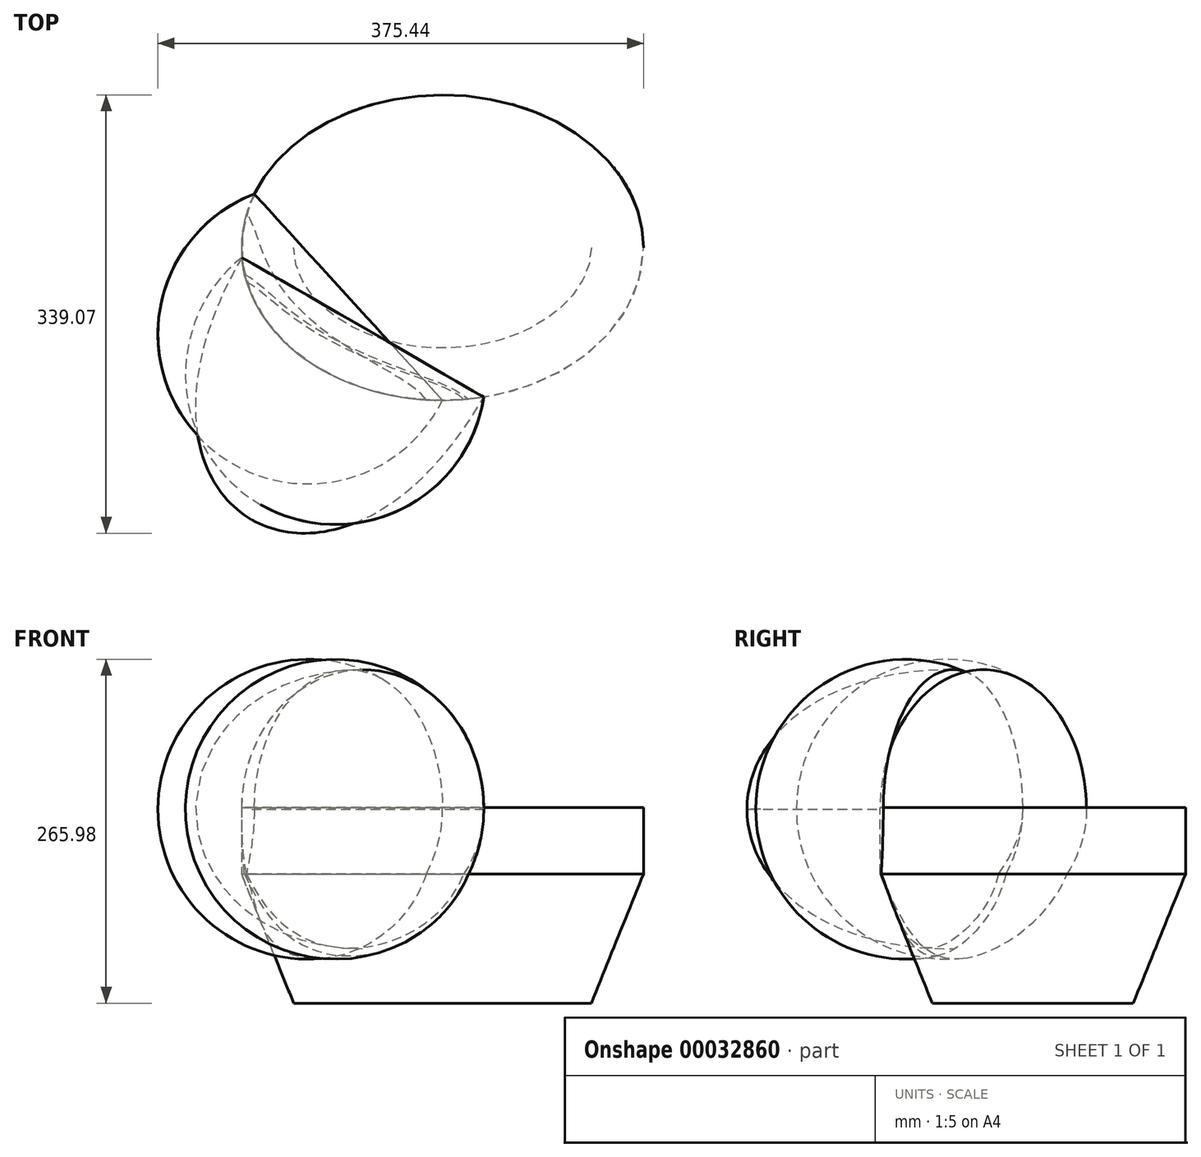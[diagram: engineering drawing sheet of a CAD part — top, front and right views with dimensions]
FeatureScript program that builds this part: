
annotation { "Feature Type Name" : "Feature", "Feature Type Description" : "" }
export const myFeature = defineFeature(function(context is Context, id is Id, definition is map)
    precondition{}
    {
        {
            assignVariable(context, id + "F0", {"name" : "DCM", "anyValue" : 21.6});
        }
        {
            var Q0;
            Q0=qCreatedBy(makeId("Top.planeOp"),FACE);
            var sketch = newSketch(context, id + "F1", { "sketchPlane" : qUnion([Q0])});
            skEllipse(sketch, "E0", {"center": v(0, 0) * mm, "majorRadius": 155.45 * mm, "minorRadius": 118.11 * mm, "majorAxis": v(1, 0)});
            skSolve(sketch);
        }
        {
            var Q0;
            Q0=qCreatedBy(makeId("Top.planeOp"),FACE);
            var sketch = newSketch(context, id + "F2", { "sketchPlane" : qUnion([Q0])});
            skEllipse(sketch, "E1", {"center": v(0, 0) * mm, "majorRadius": 155.45 * mm, "minorRadius": 118.11 * mm, "majorAxis": v(-1, 0)});
            skLineSegment(sketch, "E2", {"start": v(0, 0) * mm, "end": v(-177.32, -177.32) * mm, "construction": true});
            skLineSegment(sketch, "E3", {"start": v(-155.13, -7.6) * mm, "end": v(31.94, -115.6) * mm});
            skPoint(sketch, "E4", {"position": v(-61.6, -61.6) * mm});
            skEllipse(sketch, "E5", {"center": v(-61.6, -61.6) * mm, "majorRadius": 53 * mm, "minorRadius": 22.7 * mm, "majorAxis": v(-0.87, 0.5), "construction": true});
            skLineSegment(sketch, "E6", {"start": v(-61.6, -61.6) * mm, "end": v(-147.52, -210.43) * mm});
            skPoint(sketch, "E7", {"position": v(-94.04, -94.04) * mm});
            skFitSpline(sketch, "E8", {"points": [v(-155.13, -7.6) * mm, v(31.94, -115.6) * mm], "startDerivative": vector(-343.7, -595.35) * mm, "endDerivative": vector(343.7, 595.35) * mm});
            skLineSegment(sketch, "E9", {"start": v(-269.7, -206.05) * mm, "end": v(-82.63, -314.04) * mm, "construction": true});
            skSolve(sketch);
        }
        {
            var Q0;
            Q0=qCreatedBy(makeId("Top.planeOp"),FACE);
            var sketch = newSketch(context, id + "F3", { "sketchPlane" : qUnion([Q0])});
            skArc(sketch, "E10", {"start": v(-155.13, -7.6) * mm, "mid": v(-140.72, -198.65) * mm, "end": v(31.94, -115.6) * mm});
            skLineSegment(sketch, "E11", {"start": v(-155.13, -7.6) * mm, "end": v(31.94, -115.6) * mm});
            skLineSegment(sketch, "E12", {"start": v(-61.6, -61.6) * mm, "end": v(-140.72, -198.65) * mm});
            skSolve(sketch);
        }
        {
            var Q0;
            Q0=qCreatedBy(makeId("Top.planeOp"),FACE);
            var sketch = newSketch(context, id + "F4", { "sketchPlane" : qUnion([Q0])});
            skLineSegment(sketch, "E13", {"start": v(0, 0) * mm, "end": v(0, -196.63) * mm, "construction": true});
            skLineSegment(sketch, "E14", {"start": v(0, -118.11) * mm, "end": v(-145.54, 41.5) * mm});
            skLineSegment(sketch, "E15", {"start": v(-72.77, -38.3) * mm, "end": v(-189.7, -144.93) * mm});
            skArc(sketch, "E16", {"start": v(-145.54, 41.5) * mm, "mid": v(-189.7, -144.93) * mm, "end": v(0, -118.11) * mm});
            skSolve(sketch);
        }
        {
            var Q0;
            Q0=makeQuery(id+"F1.imprint","IMPRINT",FACE,{"disambiguationData":[TD([[makeQuery(id+"F1.imprint","IMPRINT",EDGE,{"derivedFrom":sQuery(id+"F1.wireOp",EDGE,"E0")}),1.0]])]});
            extrude(context, id + "F5", {"entities" : qUnion([Q0]), "depth" : (getVariable(context, 'DCM') + 2) / 20 * mm, "hasSecondDirection" : true, "secondDirectionOppositeDirection" : true, "secondDirectionDepth" : 50 * mm});
        }
        {
            var Q0;
            Q0=makeQuery(id+"F5.opExtrude","CAP_FACE",FACE,{"disambiguationData":[OSD([sQuery(id+"F1.wireOp",EDGE,"E0")])],"isStart":true});
            extrude(context, id + "F6", {"entities" : qUnion([Q0]), "operationType" : NewBodyOperationType.ADD, "depth" : 100 * mm, "hasDraft" : true, "draftAngle" : 22 * degree, "draftPullDirection" : true});
        }
        {
            var Q0;
            {var subQ0=sQuery(id+"F2.wireOp",EDGE,"E6");var subQ3=sQuery(id+"F2.wireOp",EDGE,"E3");var subQ4=makeQuery(id+"F2.imprint","INTERSECT",VERTEX,{"derivedFrom":[subQ3,subQ0]});Q0=makeQuery(id+"F2.imprint","IMPRINT",FACE,{"disambiguationData":[TD([[makeQuery(id+"F2.imprint","IMPRINT",EDGE,{"disambiguationData":[TD([[subQ4,-1.0]])],"derivedFrom":subQ0}),1.0]])]});}
            var Q1;
            {var subQ0=sQuery(id+"F2.wireOp",EDGE,"E6");var subQ3=sQuery(id+"F2.wireOp",EDGE,"E5");var subQ4=makeQuery(id+"F2.imprint","INTERSECT",VERTEX,{"derivedFrom":[subQ3,subQ0]});Q1=makeQuery(id+"F2.imprint","IMPRINT",FACE,{"disambiguationData":[TD([[makeQuery(id+"F2.imprint","IMPRINT",EDGE,{"disambiguationData":[TD([[subQ4,1.0]])],"derivedFrom":subQ0}),1.0]])]});}
            var Q2;
            {var subQ2=sQuery(id+"F2.wireOp",EDGE,"E6");var subQ4=sQuery(id+"F2.wireOp",EDGE,"E1");var subQ6=makeQuery(id+"F2.imprint","INTERSECT",VERTEX,{"derivedFrom":[subQ4,subQ2]});Q2=makeQuery(id+"F2.imprint","IMPRINT",FACE,{"disambiguationData":[TD([[makeQuery(id+"F2.imprint","IMPRINT",EDGE,{"disambiguationData":[TD([[subQ6,-1.0]])],"derivedFrom":subQ2}),1.0]])]});}
            var Q3;
            Q3=sQuery(id+"F2.wireOp",EDGE,"E6");
            revolve(context, id + "F7", {"entities" : qUnion([Q0, Q1, Q2]), "axis" : qUnion([Q3]), "revolveType" : RevolveType.FULL});
        }
        {
            var Q0;
            {var subQ0=sQuery(id+"F3.wireOp",EDGE,"E12");Q0=makeQuery(id+"F3.imprint","IMPRINT",FACE,{"disambiguationData":[TD([[makeQuery(id+"F3.imprint","IMPRINT",EDGE,{"derivedFrom":subQ0}),1.0]])]});}
            var Q1;
            Q1=sQuery(id+"F3.wireOp",EDGE,"E12");
            revolve(context, id + "F8", {"entities" : qUnion([Q0]), "axis" : qUnion([Q1]), "revolveType" : RevolveType.FULL});
        }
        {
            var Q0;
            {var subQ3=sQuery(id+"F4.wireOp",EDGE,"E15");Q0=makeQuery(id+"F4.imprint","IMPRINT",FACE,{"disambiguationData":[TD([[makeQuery(id+"F4.imprint","IMPRINT",EDGE,{"derivedFrom":subQ3}),-1.0]])]});}
            var Q1;
            Q1=sQuery(id+"F4.wireOp",EDGE,"E15");
            revolve(context, id + "F9", {"entities" : qUnion([Q0]), "axis" : qUnion([Q1]), "revolveType" : RevolveType.FULL});
        }
        {
            var Q0;
            Q0=makeQuery(id+"F5.opExtrude","SWEPT_BODY",BODY,{"disambiguationData":[OSD([sQuery(id+"F1.wireOp",EDGE,"E0")])]});
            var Q1;
            Q1=makeQuery(id+"F7.opRevolve","SWEPT_BODY",BODY,{"disambiguationData":[OSD([sQuery(id+"F2.wireOp",EDGE,"E3"),sQuery(id+"F2.wireOp",EDGE,"E6"),sQuery(id+"F2.wireOp",EDGE,"E8")])]});
            var Q2;
            Q2=makeQuery(id+"F8.opRevolve","SWEPT_BODY",BODY,{"disambiguationData":[OSD([sQuery(id+"F3.wireOp",EDGE,"E10"),sQuery(id+"F3.wireOp",EDGE,"E11"),sQuery(id+"F3.wireOp",EDGE,"E12")])]});
            var Q3;
            Q3=makeQuery(id+"F9.opRevolve","SWEPT_BODY",BODY,{"disambiguationData":[OSD([sQuery(id+"F4.wireOp",EDGE,"E14"),sQuery(id+"F4.wireOp",EDGE,"E15"),sQuery(id+"F4.wireOp",EDGE,"E16")])]});
            booleanBodies(context, id + "F10", {"operationType" : BooleanOperationType.SUBTRACTION, "tools" : qUnion([Q0]), "targets" : qUnion([Q1, Q2, Q3]), "keepTools" : true});
        }
        {
            var Q0;
            Q0=sQuery(id+"F2.wireOp",EDGE,"E3");
            cPlane(context, id + "F11", {"entities" : qUnion([Q0]), "cplaneType" : CPlaneType.LINE_ANGLE, "offset" : 150 * mm, "angle" : 0 * degree, "width" : 150 * mm, "height" : 150 * mm});
        }
    });
